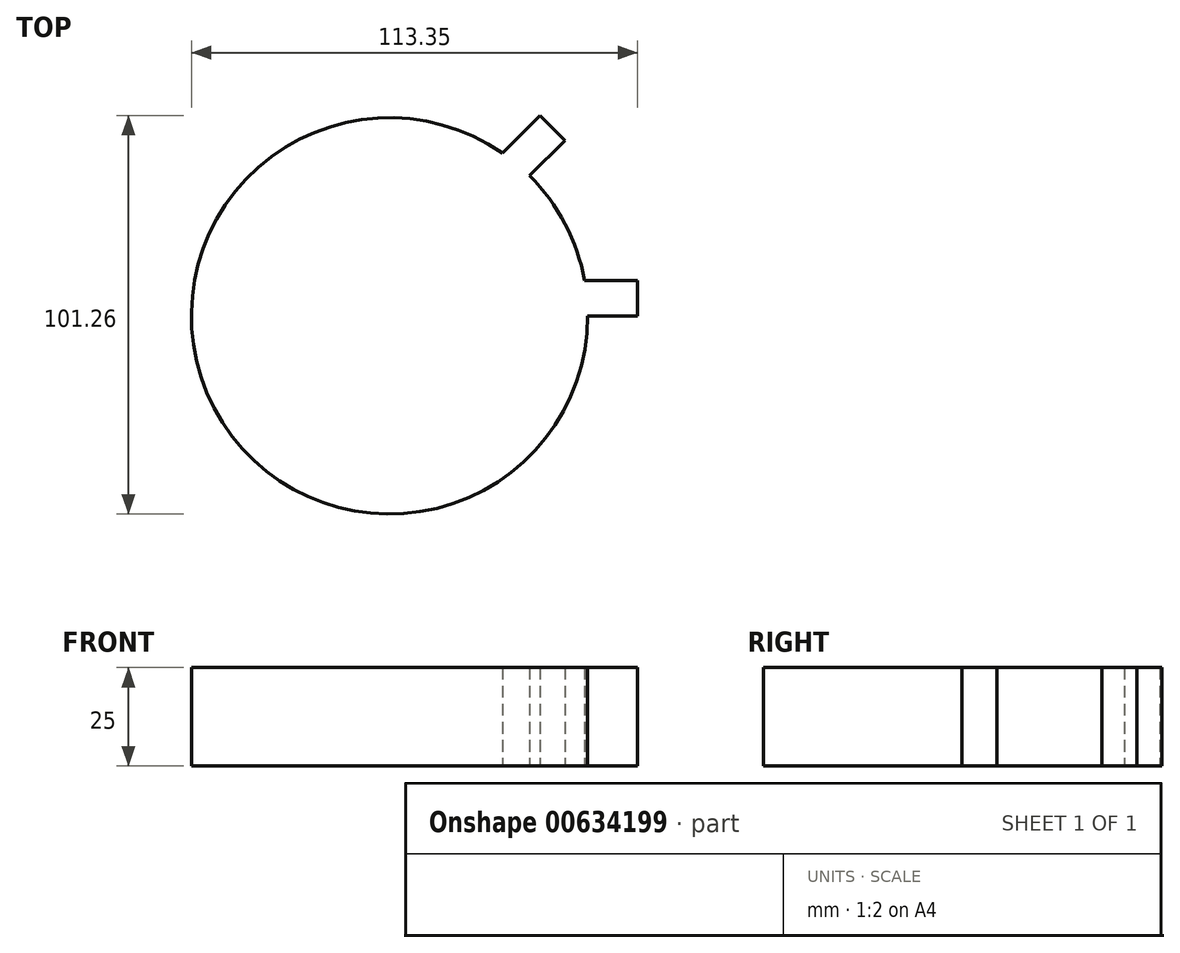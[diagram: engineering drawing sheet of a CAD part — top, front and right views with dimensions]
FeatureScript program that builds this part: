
annotation { "Feature Type Name" : "Feature", "Feature Type Description" : "" }
export const myFeature = defineFeature(function(context is Context, id is Id, definition is map)
    precondition{}
    {
        {
            var Q0;
            Q0=qCreatedBy(makeId("Top.planeOp"),FACE);
            var sketch = newSketch(context, id + "F0", { "sketchPlane" : qUnion([Q0])});
            skCircle(sketch, "E0", {"center": v(0, 0) * mm, "radius": 50.35 * mm});
            skLineSegment(sketch, "E1", {"start": v(0, 0) * mm, "end": v(63, 0) * mm});
            skLineSegment(sketch, "E2", {"start": v(0, 0) * mm, "end": v(44.55, 44.55) * mm, "construction": true});
            skLineSegment(sketch, "E3", {"start": v(0, 0) * mm, "end": v(-35.6, 35.6) * mm, "construction": true});
            skLineSegment(sketch, "E4", {"start": v(0, 0) * mm, "end": v(0, 50.35) * mm, "construction": true});
            skLineSegment(sketch, "E5", {"start": v(0, 0) * mm, "end": v(44.55, 44.55) * mm});
            skLineSegment(sketch, "E6", {"start": v(63, 0) * mm, "end": v(63, 9) * mm});
            skLineSegment(sketch, "E7", {"start": v(63, 9) * mm, "end": v(49.54, 9) * mm});
            skLineSegment(sketch, "E8", {"start": v(44.55, 44.55) * mm, "end": v(38.18, 50.91) * mm});
            skLineSegment(sketch, "E9", {"start": v(38.18, 50.91) * mm, "end": v(28.67, 41.4) * mm});
            skSolve(sketch);
        }
        {
            var Q0;
            {var subQ0=sQuery(id+"F0.wireOp",EDGE,"E5");var subQ1=sQuery(id+"F0.wireOp",EDGE,"E0");var subQ2=makeQuery(id+"F0.imprint","INTERSECT",VERTEX,{"disambiguationData":[OD(0.0)],"derivedFrom":[subQ1,subQ0]});Q0=makeQuery(id+"F0.imprint","IMPRINT",FACE,{"disambiguationData":[TD([[makeQuery(id+"F0.imprint","IMPRINT",EDGE,{"disambiguationData":[TD([[subQ2,-1.0]])],"derivedFrom":subQ1}),1.0]])]});}
            var Q1;
            {var subQ3=sQuery(id+"F0.wireOp",EDGE,"E0");var subQ6=makeQuery(id+"F0.imprint","INTERSECT",VERTEX,{"derivedFrom":[subQ3,sQuery(id+"F0.wireOp",EDGE,"E7")]});Q1=makeQuery(id+"F0.imprint","IMPRINT",FACE,{"disambiguationData":[TD([[makeQuery(id+"F0.imprint","IMPRINT",EDGE,{"disambiguationData":[TD([[subQ6,1.0]])],"derivedFrom":subQ3}),1.0]])]});}
            var Q2;
            {var subQ0=sQuery(id+"F0.wireOp",EDGE,"E0");var subQ1=sQuery(id+"F0.wireOp",EDGE,"E0");var subQ5=makeQuery(id+"F0.imprint","INTERSECT",VERTEX,{"disambiguationData":[OD(0.0)],"derivedFrom":[subQ1,subQ0]});Q2=makeQuery(id+"F0.imprint","IMPRINT",FACE,{"disambiguationData":[TD([[makeQuery(id+"F0.imprint","IMPRINT",EDGE,{"disambiguationData":[TD([[subQ5,-1.0]])],"derivedFrom":subQ1}),1.0]])]});}
            var Q3;
            {var subQ0=sQuery(id+"F0.wireOp",EDGE,"E3");Q3=makeQuery(id+"F0.imprint","IMPRINT",FACE,{"disambiguationData":[TD([[makeQuery(id+"F0.imprint","IMPRINT",EDGE,{"derivedFrom":subQ0}),-1.0]])]});}
            var Q4;
            {var subQ5=sQuery(id+"F0.wireOp",EDGE,"E3");Q4=makeQuery(id+"F0.imprint","IMPRINT",FACE,{"disambiguationData":[TD([[makeQuery(id+"F0.imprint","IMPRINT",EDGE,{"derivedFrom":subQ5}),1.0]])]});}
            var Q5;
            {var subQ4=sQuery(id+"F0.wireOp",EDGE,"E6");Q5=makeQuery(id+"F0.imprint","IMPRINT",FACE,{"disambiguationData":[TD([[makeQuery(id+"F0.imprint","IMPRINT",EDGE,{"derivedFrom":subQ4}),1.0]])]});}
            var Q6;
            {var subQ0=sQuery(id+"F0.wireOp",EDGE,"E1");var subQ1=sQuery(id+"F0.wireOp",EDGE,"E0");var subQ2=makeQuery(id+"F0.imprint","INTERSECT",VERTEX,{"derivedFrom":[subQ1,subQ0]});Q6=makeQuery(id+"F0.imprint","IMPRINT",FACE,{"disambiguationData":[TD([[makeQuery(id+"F0.imprint","IMPRINT",EDGE,{"disambiguationData":[TD([[subQ2,1.0]])],"derivedFrom":subQ1}),1.0]])]});}
            var Q7;
            {var subQ4=sQuery(id+"F0.wireOp",EDGE,"E8");Q7=makeQuery(id+"F0.imprint","IMPRINT",FACE,{"disambiguationData":[TD([[makeQuery(id+"F0.imprint","IMPRINT",EDGE,{"derivedFrom":subQ4}),1.0]])]});}
            var Q8;
            {var subQ0=sQuery(id+"F0.wireOp",EDGE,"E4");var subQ1=sQuery(id+"F0.wireOp",EDGE,"E0");var subQ2=makeQuery(id+"F0.imprint","INTERSECT",VERTEX,{"derivedFrom":[subQ1,subQ0]});Q8=makeQuery(id+"F0.imprint","IMPRINT",FACE,{"disambiguationData":[TD([[makeQuery(id+"F0.imprint","IMPRINT",EDGE,{"disambiguationData":[TD([[subQ2,-1.0]])],"derivedFrom":subQ1}),1.0]])]});}
            var Q9;
            {var subQ0=sQuery(id+"F0.wireOp",EDGE,"E0");var subQ1=sQuery(id+"F0.wireOp",EDGE,"E0");var subQ2=makeQuery(id+"F0.imprint","INTERSECT",VERTEX,{"disambiguationData":[OD(0.0)],"derivedFrom":[subQ1,subQ0]});Q9=makeQuery(id+"F0.imprint","IMPRINT",FACE,{"disambiguationData":[TD([[makeQuery(id+"F0.imprint","IMPRINT",EDGE,{"disambiguationData":[TD([[subQ2,-1.0]])],"derivedFrom":subQ1}),-1.0]])]});}
            var Q10;
            {var subQ0=sQuery(id+"F0.wireOp",EDGE,"E4");var subQ1=sQuery(id+"F0.wireOp",EDGE,"E0");var subQ2=makeQuery(id+"F0.imprint","INTERSECT",VERTEX,{"disambiguationData":[OD(0.0)],"derivedFrom":[subQ1,subQ0]});Q10=makeQuery(id+"F0.imprint","IMPRINT",FACE,{"disambiguationData":[TD([[makeQuery(id+"F0.imprint","IMPRINT",EDGE,{"disambiguationData":[TD([[subQ2,1.0]])],"derivedFrom":subQ1}),1.0]])]});}
            extrude(context, id + "F1", {"entities" : qUnion([Q0, Q1, Q2, Q3, Q4, Q5, Q6, Q7, Q8, Q9, Q10]), "depth" : 25 * mm, "offsetDistance" : 25 * mm});
        }
    });
